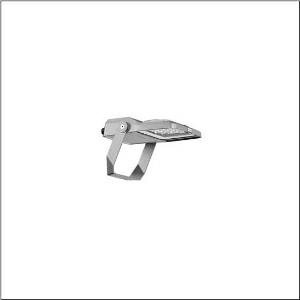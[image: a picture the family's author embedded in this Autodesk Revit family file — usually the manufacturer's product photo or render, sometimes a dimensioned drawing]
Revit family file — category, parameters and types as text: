
# Revit family: floodlight_fl_21_micro___rs12_5xa7761a4b1a_2e46
name_source: partatom
category: Lighting Fixtures
units: mm (PartAtom-declared; Revit-internal decimal feet)

## family parameters
Cut with Voids When Loaded = No
Host = Face
Light Source = No
Part Type = Normal
Room Calculation Point = No
Round Connector Dimension = Use Diameter
Shared = No

## types (1)
- --- (1 x LED, 3220 lm, 23.1 W, 4000K)
    Apparent Load = 23 VA
    CIE Flux Codes = 79 92 99 100 100
    Color Rendering = 70
    Color Temperature = 4000K
    Default Elevation = 1800 mm
    Description = Floodlight FL 21 micro, floodlight, primary light control with lens, of PMMA, primary optical cover: protective disc, of toughened safety glass, transparent, light distribution: RS12, light emission: direct distribution, installation type: surface-mounted, LED, High Power LED, rated luminous flux: 3.220lm, luminous efficacy: 139lm/W, light colour: 740, colour temperature: 4000K, control gear: ECG iQ, control: optimised constant luminous flux control (CLO 2.0), Desk-Remote (wireless, voltage-free reading and setting of iQ features in the workshop via application-optimized NFC function/RFID function), Light-Fading, Smart-Wire, Night-Set, Lumen-Switch, Temp-Guard, Auto-Match, with terminal, 6-pole, mains connection: 220..240V, AC, 50/60Hz, start of lifetime: 23W, end of lifetime: 24W, reduction: 11W, luminaire housing, of diecast aluminium, powder-coated, Siteco® metallic grey (DB 702S), corrosivity category C5 according to DIN EN ISO 12944, mounting bracket, of steel, galvanised, powder-coated, Siteco® metallic grey (DB 702S), protection rating (complete): IP66, insulation class (complete): insulation class II (safety insulation), certification: CE, protection symbol: D, impact resistance: IK07, permissible operating ambient temperature: -40..+40°C, permissible operating ambient temperature for outdoor applications: -40..+50°C, standard: DIN EN 12944, packaging unit: 1 piece

Light Distribution: RS12
    Height = 65 mm
    Lamp = 1 x LED
    Lamp Light Flux = 3220 lm
    Lamp Power = 23.1 W
    Lamp count = 1
    Length = 312 mm
    Luminous efficacy = 139 lm/W
    Manufacturer = Siteco
    ModVariant = No
    Model = 5XA7761A4B1A
    Number of Poles = 1
    OnlyDefault = Yes
    Power Factor = 1
    Product Name = Floodlight FL 21 micro | RS12
    Product group = floodlight | pylon top
    ProductGroupID = 6101
    Protection Class = Protection class II
    Protection Degree = IP 66
    RLX_Detail_Level = 1
    RlxData = <blob elided: 75137 chars, md5=0a01ffd1>
    Socket = socket
    Standby Power = 0 W
    System Light Flux = 3220 lm
    System Power = 23 W
    Type Comments = factory setting: luminous flux: 100 % | dim-lin: 254 | 455 mA
    Type Image = l_1006880.jpg
    URL = http://relux.com
    VarID = @adj_095535
    Voltage = 0 V
    Weight = 0.00 kg
    Width = 230 mm

## geometry (parser evidence)
native form markers: Blend x4, Sweep x12
no freeform markers — native parametric forms only
